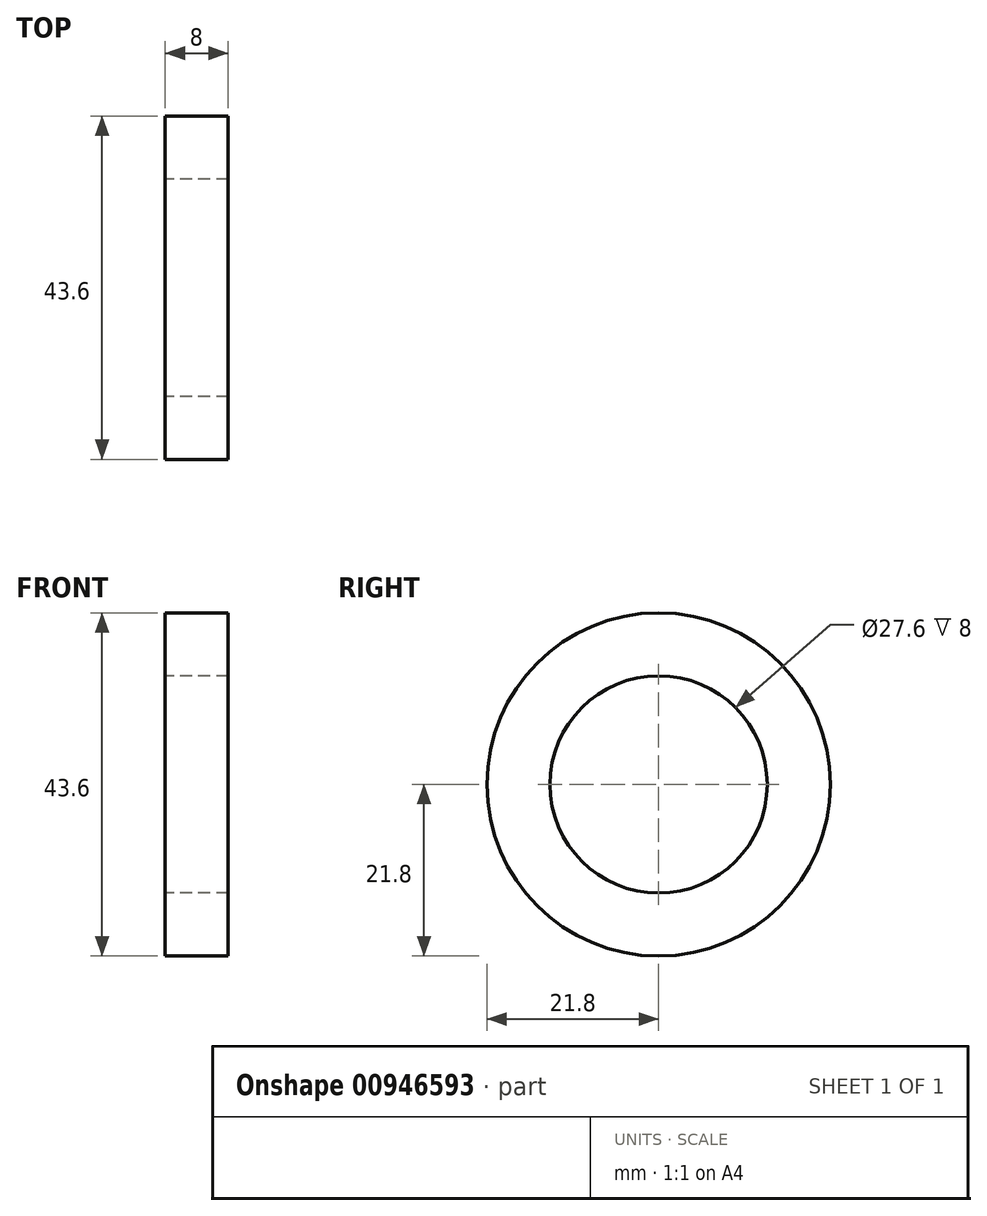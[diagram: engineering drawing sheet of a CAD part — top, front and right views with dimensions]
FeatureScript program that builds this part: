
annotation { "Feature Type Name" : "Feature", "Feature Type Description" : "" }
export const myFeature = defineFeature(function(context is Context, id is Id, definition is map)
    precondition{}
    {
        {
            var Q0;
            Q0=qCreatedBy(makeId("Top.planeOp"),FACE);
            var sketch = newSketch(context, id + "F0", { "sketchPlane" : qUnion([Q0])});
            skLineSegment(sketch, "E0", {"start": v(-36.2, 0) * mm, "end": v(47.4, 0) * mm, "construction": true});
            skLineSegment(sketch, "E1.bottom", {"start": v(-3.4, 13.8) * mm, "end": v(4.6, 13.8) * mm});
            skLineSegment(sketch, "E1.top", {"start": v(-3.4, 21.8) * mm, "end": v(4.6, 21.8) * mm});
            skLineSegment(sketch, "E1.left", {"start": v(-3.4, 13.8) * mm, "end": v(-3.4, 21.8) * mm});
            skLineSegment(sketch, "E1.right", {"start": v(4.6, 13.8) * mm, "end": v(4.6, 21.8) * mm});
            skSolve(sketch);
        }
        {
            var Q0;
            Q0 = qSketchRegion(id + "F0", true);
            var Q1;
            Q1=sQuery(id+"F0.wireOp",EDGE,"E0");
            revolve(context, id + "F1", {"surfaceOperationType" : NewSurfaceOperationType.NEW, "entities" : qUnion([Q0]), "axis" : qUnion([Q1]), "revolveType" : RevolveType.FULL});
        }
    });
